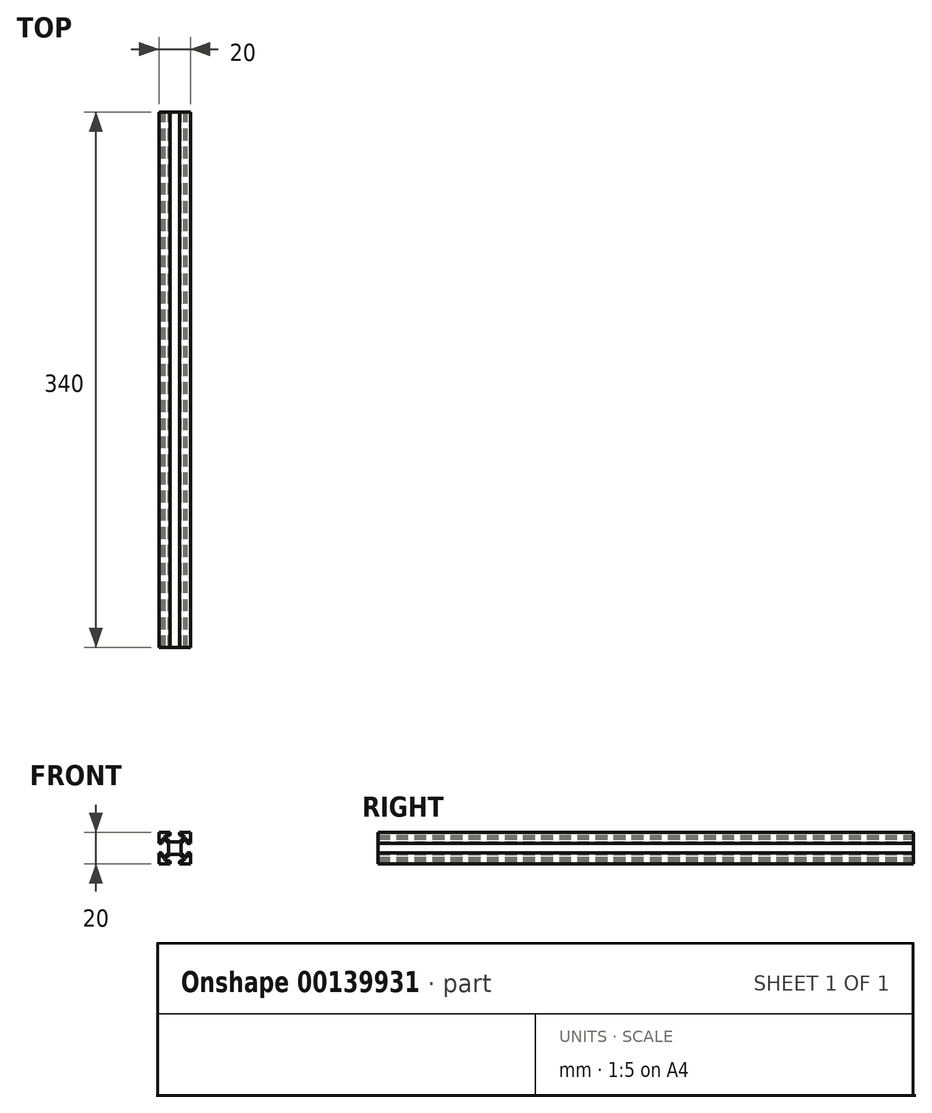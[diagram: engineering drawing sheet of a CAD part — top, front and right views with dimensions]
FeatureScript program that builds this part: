
annotation { "Feature Type Name" : "Feature", "Feature Type Description" : "" }
export const myFeature = defineFeature(function(context is Context, id is Id, definition is map)
    precondition{}
    {
        {
            var Q0;
            Q0=qCreatedBy(makeId("Front.planeOp"),FACE);
            var sketch = newSketch(context, id + "F0", { "sketchPlane" : qUnion([Q0])});
            skLineSegment(sketch, "E0", {"start": v(-48.23, 44.73) * mm, "end": v(-46.23, 44.73) * mm});
            skLineSegment(sketch, "E1", {"start": v(-46.23, 44.73) * mm, "end": v(-46.23, 47.73) * mm});
            skLineSegment(sketch, "E2", {"start": v(-46.23, 47.73) * mm, "end": v(-45.23, 47.73) * mm});
            skLineSegment(sketch, "E3", {"start": v(-45.23, 47.73) * mm, "end": v(-42.23, 44.73) * mm});
            skLineSegment(sketch, "E4", {"start": v(-42.23, 44.73) * mm, "end": v(-42.23, 38.73) * mm});
            skLineSegment(sketch, "E5", {"start": v(-42.23, 38.73) * mm, "end": v(-45.23, 35.73) * mm});
            skLineSegment(sketch, "E6", {"start": v(-45.23, 35.73) * mm, "end": v(-46.23, 35.73) * mm});
            skLineSegment(sketch, "E7", {"start": v(-46.23, 35.73) * mm, "end": v(-46.23, 38.73) * mm});
            skLineSegment(sketch, "E8", {"start": v(-46.23, 38.73) * mm, "end": v(-48.23, 38.73) * mm});
            skLineSegment(sketch, "E9", {"start": v(-48.23, 38.73) * mm, "end": v(-48.23, 31.73) * mm});
            skLineSegment(sketch, "E10", {"start": v(-48.23, 31.73) * mm, "end": v(-41.23, 31.73) * mm});
            skLineSegment(sketch, "E11", {"start": v(-41.23, 31.73) * mm, "end": v(-41.23, 33.73) * mm});
            skLineSegment(sketch, "E12", {"start": v(-41.23, 33.73) * mm, "end": v(-44.23, 33.73) * mm});
            skLineSegment(sketch, "E13", {"start": v(-44.23, 33.73) * mm, "end": v(-44.23, 34.73) * mm});
            skLineSegment(sketch, "E14", {"start": v(-44.23, 34.73) * mm, "end": v(-41.23, 37.73) * mm});
            skLineSegment(sketch, "E15", {"start": v(-41.23, 37.73) * mm, "end": v(-35.23, 37.73) * mm});
            skLineSegment(sketch, "E16", {"start": v(-35.23, 37.73) * mm, "end": v(-32.23, 34.73) * mm});
            skLineSegment(sketch, "E17", {"start": v(-32.23, 34.73) * mm, "end": v(-32.23, 33.73) * mm});
            skLineSegment(sketch, "E18", {"start": v(-32.23, 33.73) * mm, "end": v(-35.23, 33.73) * mm});
            skLineSegment(sketch, "E19", {"start": v(-35.23, 33.73) * mm, "end": v(-35.23, 31.73) * mm});
            skLineSegment(sketch, "E20", {"start": v(-35.23, 31.73) * mm, "end": v(-28.23, 31.73) * mm});
            skLineSegment(sketch, "E21", {"start": v(-28.23, 31.73) * mm, "end": v(-28.23, 38.73) * mm});
            skLineSegment(sketch, "E22", {"start": v(-28.23, 38.73) * mm, "end": v(-30.23, 38.73) * mm});
            skLineSegment(sketch, "E23", {"start": v(-30.23, 38.73) * mm, "end": v(-30.23, 35.73) * mm});
            skLineSegment(sketch, "E24", {"start": v(-30.23, 35.73) * mm, "end": v(-31.23, 35.73) * mm});
            skLineSegment(sketch, "E25", {"start": v(-31.23, 35.73) * mm, "end": v(-34.23, 38.73) * mm});
            skLineSegment(sketch, "E26", {"start": v(-34.23, 38.73) * mm, "end": v(-34.23, 44.73) * mm});
            skLineSegment(sketch, "E27", {"start": v(-34.23, 44.73) * mm, "end": v(-31.23, 47.73) * mm});
            skLineSegment(sketch, "E28", {"start": v(-31.23, 47.73) * mm, "end": v(-30.23, 47.73) * mm});
            skLineSegment(sketch, "E29", {"start": v(-30.23, 47.73) * mm, "end": v(-30.23, 44.73) * mm});
            skLineSegment(sketch, "E30", {"start": v(-30.23, 44.73) * mm, "end": v(-28.23, 44.73) * mm});
            skLineSegment(sketch, "E31", {"start": v(-28.23, 44.73) * mm, "end": v(-28.23, 51.73) * mm});
            skLineSegment(sketch, "E32", {"start": v(-28.23, 51.73) * mm, "end": v(-35.23, 51.73) * mm});
            skLineSegment(sketch, "E33", {"start": v(-35.23, 51.73) * mm, "end": v(-35.23, 49.73) * mm});
            skLineSegment(sketch, "E34", {"start": v(-35.23, 49.73) * mm, "end": v(-32.23, 49.73) * mm});
            skLineSegment(sketch, "E35", {"start": v(-32.23, 49.73) * mm, "end": v(-32.23, 48.73) * mm});
            skLineSegment(sketch, "E36", {"start": v(-32.23, 48.73) * mm, "end": v(-35.23, 45.73) * mm});
            skLineSegment(sketch, "E37", {"start": v(-35.23, 45.73) * mm, "end": v(-41.23, 45.73) * mm});
            skLineSegment(sketch, "E38", {"start": v(-41.23, 45.73) * mm, "end": v(-44.23, 48.73) * mm});
            skLineSegment(sketch, "E39", {"start": v(-44.23, 48.73) * mm, "end": v(-44.23, 49.73) * mm});
            skLineSegment(sketch, "E40", {"start": v(-44.23, 49.73) * mm, "end": v(-41.23, 49.73) * mm});
            skLineSegment(sketch, "E41", {"start": v(-41.23, 49.73) * mm, "end": v(-41.23, 51.73) * mm});
            skLineSegment(sketch, "E42", {"start": v(-41.23, 51.73) * mm, "end": v(-48.23, 51.73) * mm});
            skLineSegment(sketch, "E43", {"start": v(-48.23, 51.73) * mm, "end": v(-48.23, 44.73) * mm});
            skSolve(sketch);
        }
        {
            var Q0;
            Q0 = qSketchRegion(id + "F0", true);
            extrude(context, id + "F1", {"entities" : qUnion([Q0]), "depth" : 340 * mm, "offsetDistance" : 25 * mm});
        }
    });
